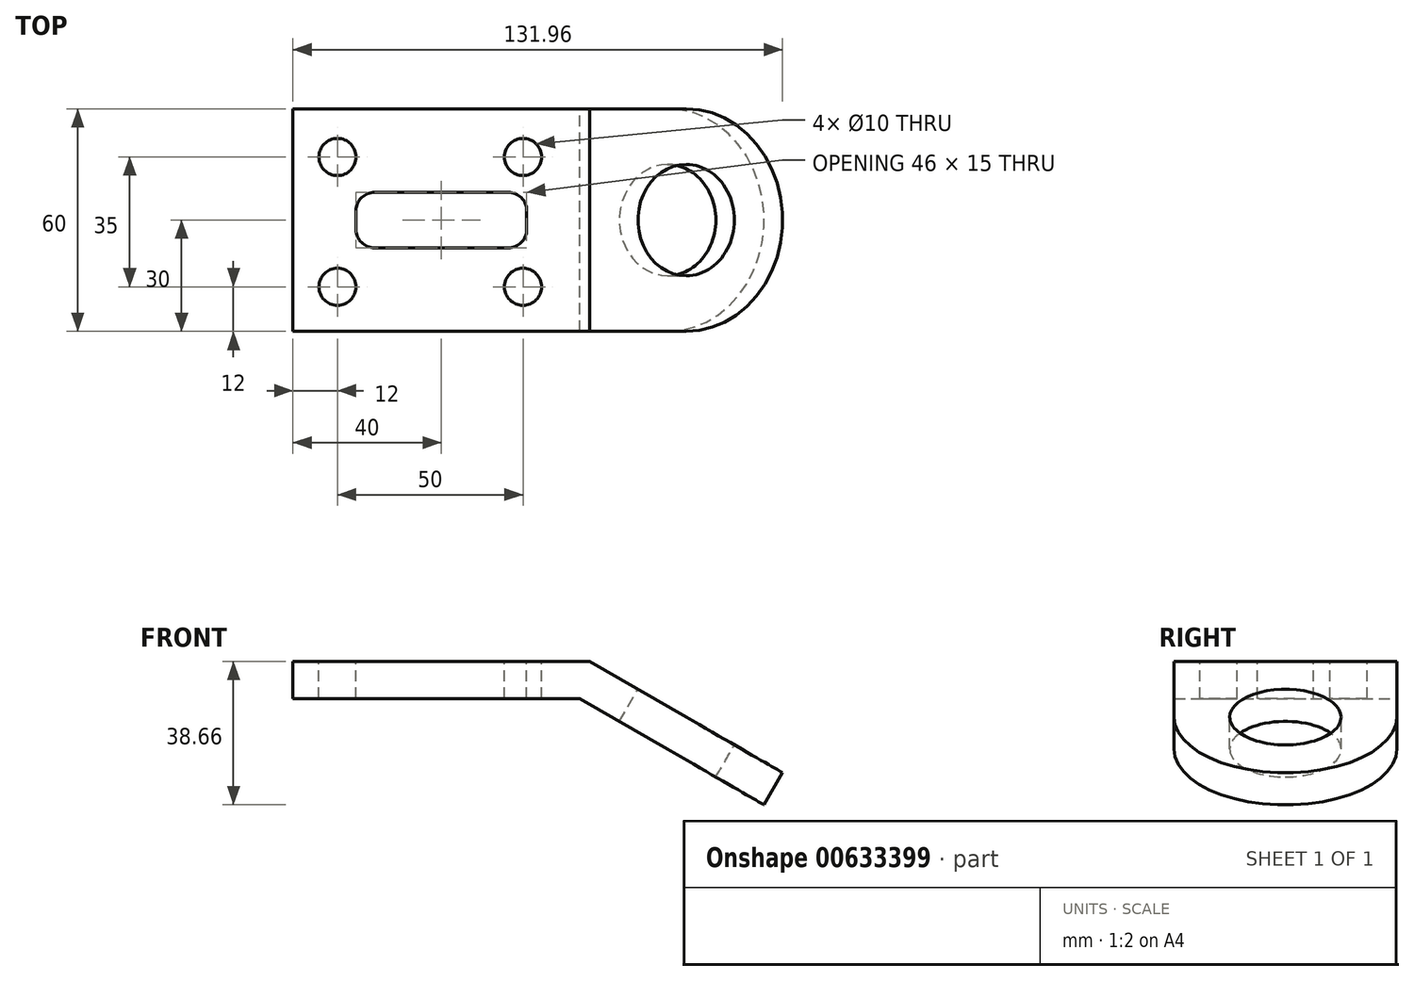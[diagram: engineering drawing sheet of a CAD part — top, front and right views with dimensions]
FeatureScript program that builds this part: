
annotation { "Feature Type Name" : "Feature", "Feature Type Description" : "" }
export const myFeature = defineFeature(function(context is Context, id is Id, definition is map)
    precondition{}
    {
        {
            var Q0;
            Q0=qCreatedBy(makeId("Front.planeOp"),FACE);
            var sketch = newSketch(context, id + "F0", { "sketchPlane" : qUnion([Q0])});
            skLineSegment(sketch, "E0", {"start": v(0, 0) * mm, "end": v(80, 0) * mm});
            skLineSegment(sketch, "E1", {"start": v(80, 0) * mm, "end": v(131.96, -30) * mm});
            skLineSegment(sketch, "E2.0", {"start": v(77.32, -10) * mm, "end": v(126.96, -38.66) * mm});
            skLineSegment(sketch, "E2.1", {"start": v(0, -10) * mm, "end": v(77.32, -10) * mm});
            skLineSegment(sketch, "E3", {"start": v(0, 0) * mm, "end": v(0, -10) * mm});
            skLineSegment(sketch, "E4", {"start": v(131.96, -30) * mm, "end": v(126.96, -38.66) * mm});
            skSolve(sketch);
        }
        {
            var Q0;
            Q0=makeQuery(id+"F0.imprint","IMPRINT",FACE,{"disambiguationData":[TD([[makeQuery(id+"F0.imprint","IMPRINT",EDGE,{"derivedFrom":sQuery(id+"F0.wireOp",EDGE,"E0")}),-1.0]])]});
            extrude(context, id + "F1", {"entities" : qUnion([Q0]), "depth" : 60 * mm, "offsetDistance" : 25 * mm});
        }
        {
            var Q0;
            Q0=makeQuery(id+"F1.opExtrude","CAP_EDGE",EDGE,{"disambiguationData":[OSD([sQuery(id+"F0.wireOp",EDGE,"E4")])],"isStart":true});
            var Q1;
            Q1=makeQuery(id+"F1.opExtrude","CAP_EDGE",EDGE,{"disambiguationData":[OSD([sQuery(id+"F0.wireOp",EDGE,"E4")])],"isStart":false});
            fillet(context, id + "F2", {"entities" : qUnion([Q0, Q1]), "radius" : 30 * mm, "tangentPropagation" : true, "allowEdgeOverflow" : false});
        }
        {
            var Q0;
            Q0=makeQuery(id+"F1.opExtrude","SWEPT_FACE",FACE,{"disambiguationData":[OSD([sQuery(id+"F0.wireOp",EDGE,"E1")])]});
            var sketch = newSketch(context, id + "F3", { "sketchPlane" : qUnion([Q0])});
            skCircle(sketch, "E5", {"center": v(99.28, -30) * mm, "radius": 15 * mm});
            skSolve(sketch);
        }
        {
            var Q0;
            Q0=makeQuery(id+"F3.imprint","IMPRINT",FACE,{"disambiguationData":[TD([[makeQuery(id+"F3.imprint","IMPRINT",EDGE,{"derivedFrom":sQuery(id+"F3.wireOp",EDGE,"E5")}),1.0]])]});
            extrude(context, id + "F4", {"entities" : qUnion([Q0]), "operationType" : NewBodyOperationType.REMOVE, "endBound" : BoundingType.UP_TO_NEXT, "oppositeDirection" : true, "depth" : 25 * mm, "offsetDistance" : 25 * mm});
        }
        {
            var Q0;
            Q0=makeQuery(id+"F1.opExtrude","SWEPT_FACE",FACE,{"disambiguationData":[OSD([sQuery(id+"F0.wireOp",EDGE,"E0")])]});
            var sketch = newSketch(context, id + "F5", { "sketchPlane" : qUnion([Q0])});
            skCircle(sketch, "E6", {"center": v(12, -48) * mm, "radius": 5 * mm});
            skCircle(sketch, "E7.0.1.0", {"center": v(12, -13) * mm, "radius": 5 * mm});
            skCircle(sketch, "E7.1.0.0", {"center": v(62, -48) * mm, "radius": 5 * mm});
            skCircle(sketch, "E7.1.1.0", {"center": v(62, -13) * mm, "radius": 5 * mm});
            skLineSegment(sketch, "E7.direction1", {"start": v(12, -48) * mm, "end": v(62, -48) * mm, "construction": true});
            skLineSegment(sketch, "E7.direction2", {"start": v(12, -48) * mm, "end": v(12, -13) * mm, "construction": true});
            skSolve(sketch);
        }
        {
            var Q0;
            Q0=makeQuery(id+"F5.imprint","IMPRINT",FACE,{"disambiguationData":[TD([[makeQuery(id+"F5.imprint","IMPRINT",EDGE,{"derivedFrom":sQuery(id+"F5.wireOp",EDGE,"E7.0.1.0")}),1.0]])]});
            var Q1;
            Q1=makeQuery(id+"F5.imprint","IMPRINT",FACE,{"disambiguationData":[TD([[makeQuery(id+"F5.imprint","IMPRINT",EDGE,{"derivedFrom":sQuery(id+"F5.wireOp",EDGE,"E6")}),1.0]])]});
            var Q2;
            Q2=makeQuery(id+"F5.imprint","IMPRINT",FACE,{"disambiguationData":[TD([[makeQuery(id+"F5.imprint","IMPRINT",EDGE,{"derivedFrom":sQuery(id+"F5.wireOp",EDGE,"E7.1.0.0")}),1.0]])]});
            var Q3;
            Q3=makeQuery(id+"F5.imprint","IMPRINT",FACE,{"disambiguationData":[TD([[makeQuery(id+"F5.imprint","IMPRINT",EDGE,{"derivedFrom":sQuery(id+"F5.wireOp",EDGE,"E7.1.1.0")}),1.0]])]});
            extrude(context, id + "F6", {"entities" : qUnion([Q0, Q1, Q2, Q3]), "operationType" : NewBodyOperationType.REMOVE, "endBound" : BoundingType.UP_TO_NEXT, "oppositeDirection" : true, "depth" : 25 * mm, "offsetDistance" : 25 * mm});
        }
        {
            var Q0;
            Q0=makeQuery(id+"F1.opExtrude","SWEPT_FACE",FACE,{"disambiguationData":[OSD([sQuery(id+"F0.wireOp",EDGE,"E0")])]});
            var sketch = newSketch(context, id + "F7", { "sketchPlane" : qUnion([Q0])});
            skLineSegment(sketch, "E8.bottom", {"start": v(63, -37.5) * mm, "end": v(17, -37.5) * mm});
            skLineSegment(sketch, "E8.top", {"start": v(63, -22.5) * mm, "end": v(17, -22.5) * mm});
            skLineSegment(sketch, "E8.left", {"start": v(63, -37.5) * mm, "end": v(63, -22.5) * mm});
            skLineSegment(sketch, "E8.right", {"start": v(17, -37.5) * mm, "end": v(17, -22.5) * mm});
            skPoint(sketch, "E8.middle", {"position": v(40, -30) * mm});
            skPoint(sketch, "E8.middle.positionSnap0", {"position": v(0, -30) * mm});
            skPoint(sketch, "E8.middle.positionSnap1", {"position": v(40, 0) * mm});
            skPoint(sketch, "E8.centerSnap0", {"position": v(0, -30) * mm});
            skPoint(sketch, "E8.centerSnap1", {"position": v(40, 0) * mm});
            skSolve(sketch);
        }
        {
            var Q0;
            Q0 = qSketchRegion(id + "F7", true);
            extrude(context, id + "F8", {"entities" : qUnion([Q0]), "operationType" : NewBodyOperationType.REMOVE, "endBound" : BoundingType.UP_TO_NEXT, "oppositeDirection" : true, "depth" : 25 * mm, "offsetDistance" : 25 * mm});
        }
        {
            var Q0;
            Q0=makeQuery(id+"F8.boolean.opBoolean","COPY",EDGE,{"derivedFrom":makeQuery(id+"F8.opExtrude","SWEPT_EDGE",EDGE,{"disambiguationData":[OSD([sQuery(id+"F7.wireOp",EDGE,"E8.top"),sQuery(id+"F7.wireOp",EDGE,"E8.right")])]})});
            fillet(context, id + "F9", {"entities" : qUnion([Q0]), "radius" : 5 * mm, "tangentPropagation" : true, "allowEdgeOverflow" : false});
        }
        {
            var Q0;
            Q0=makeQuery(id+"F8.boolean.opBoolean","COPY",EDGE,{"derivedFrom":makeQuery(id+"F8.opExtrude","SWEPT_EDGE",EDGE,{"disambiguationData":[OSD([sQuery(id+"F7.wireOp",EDGE,"E8.top"),sQuery(id+"F7.wireOp",EDGE,"E8.left")])]})});
            var Q1;
            Q1=makeQuery(id+"F8.boolean.opBoolean","COPY",EDGE,{"derivedFrom":makeQuery(id+"F8.opExtrude","SWEPT_EDGE",EDGE,{"disambiguationData":[OSD([sQuery(id+"F7.wireOp",EDGE,"E8.bottom"),sQuery(id+"F7.wireOp",EDGE,"E8.left")])]})});
            var Q2;
            Q2=makeQuery(id+"F8.boolean.opBoolean","COPY",EDGE,{"derivedFrom":makeQuery(id+"F8.opExtrude","SWEPT_EDGE",EDGE,{"disambiguationData":[OSD([sQuery(id+"F7.wireOp",EDGE,"E8.bottom"),sQuery(id+"F7.wireOp",EDGE,"E8.right")])]})});
            fillet(context, id + "F10", {"entities" : qUnion([Q0, Q1, Q2]), "radius" : 5 * mm, "tangentPropagation" : true, "allowEdgeOverflow" : false});
        }
    });
